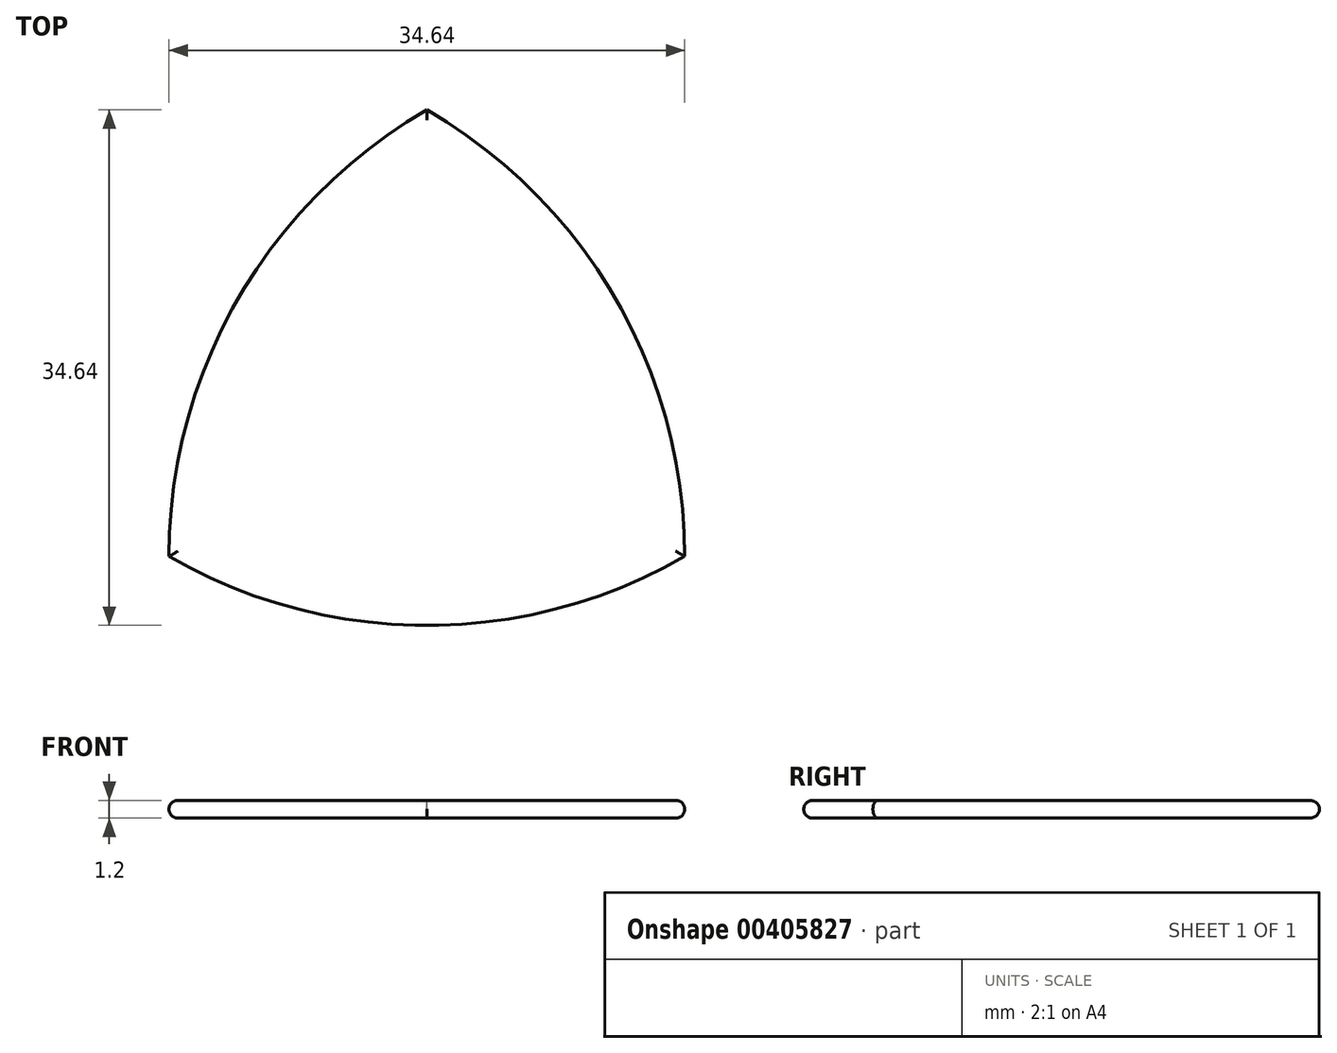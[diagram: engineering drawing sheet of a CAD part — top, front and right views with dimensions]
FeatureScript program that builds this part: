
annotation { "Feature Type Name" : "Feature", "Feature Type Description" : "" }
export const myFeature = defineFeature(function(context is Context, id is Id, definition is map)
    precondition{}
    {
        {
            var Q0;
            Q0=qCreatedBy(makeId("Top.planeOp"),FACE);
            var sketch = newSketch(context, id + "F0", { "sketchPlane" : qUnion([Q0])});
            skCircle(sketch, "E0.cCircle", {"center": v(0, 0) * mm, "radius": 20 * mm, "construction": true});
            skLineSegment(sketch, "E0.0", {"start": v(0, 20) * mm, "end": v(17.32, -10) * mm, "construction": true});
            skLineSegment(sketch, "E0.1", {"start": v(17.32, -10) * mm, "end": v(-17.32, -10) * mm, "construction": true});
            skLineSegment(sketch, "E0.2", {"start": v(-17.32, -10) * mm, "end": v(0, 20) * mm, "construction": true});
            skArc(sketch, "E1", {"start": v(-17.32, -10) * mm, "mid": v(0, -14.64) * mm, "end": v(17.32, -10) * mm});
            skArc(sketch, "E2", {"start": v(17.32, -10) * mm, "mid": v(12.68, 7.32) * mm, "end": v(0, 20) * mm});
            skArc(sketch, "E3", {"start": v(0, 20) * mm, "mid": v(-12.68, 7.32) * mm, "end": v(-17.32, -10) * mm});
            skSolve(sketch);
        }
        {
            var Q0;
            Q0=makeQuery(id+"F0.imprint","IMPRINT",FACE,{"disambiguationData":[TD([[makeQuery(id+"F0.imprint","IMPRINT",EDGE,{"derivedFrom":sQuery(id+"F0.wireOp",EDGE,"E1")}),1.0]])]});
            extrude(context, id + "F1", {"entities" : qUnion([Q0]), "depth" : 1.2 * mm, "offsetDistance" : 25 * mm});
        }
        {
            var Q0;
            Q0=makeQuery(id+"F1.opExtrude","CAP_EDGE",EDGE,{"disambiguationData":[OSD([sQuery(id+"F0.wireOp",EDGE,"E3")])],"isStart":false});
            var Q1;
            Q1=makeQuery(id+"F1.opExtrude","CAP_EDGE",EDGE,{"disambiguationData":[OSD([sQuery(id+"F0.wireOp",EDGE,"E2")])],"isStart":false});
            var Q2;
            Q2=makeQuery(id+"F1.opExtrude","CAP_EDGE",EDGE,{"disambiguationData":[OSD([sQuery(id+"F0.wireOp",EDGE,"E1")])],"isStart":false});
            var Q3;
            Q3=makeQuery(id+"F1.opExtrude","CAP_EDGE",EDGE,{"disambiguationData":[OSD([sQuery(id+"F0.wireOp",EDGE,"E3")])],"isStart":true});
            var Q4;
            Q4=makeQuery(id+"F1.opExtrude","CAP_EDGE",EDGE,{"disambiguationData":[OSD([sQuery(id+"F0.wireOp",EDGE,"E2")])],"isStart":true});
            var Q5;
            Q5=makeQuery(id+"F1.opExtrude","CAP_EDGE",EDGE,{"disambiguationData":[OSD([sQuery(id+"F0.wireOp",EDGE,"E1")])],"isStart":true});
            fillet(context, id + "F2", {"entities" : qUnion([Q0, Q1, Q2, Q3, Q4, Q5]), "tangentPropagation" : true, "radius" : .6 * mm, "defaultsChanged" : true, "vertexSettings" : [], "allowEdgeOverflow" : false});
        }
    });
